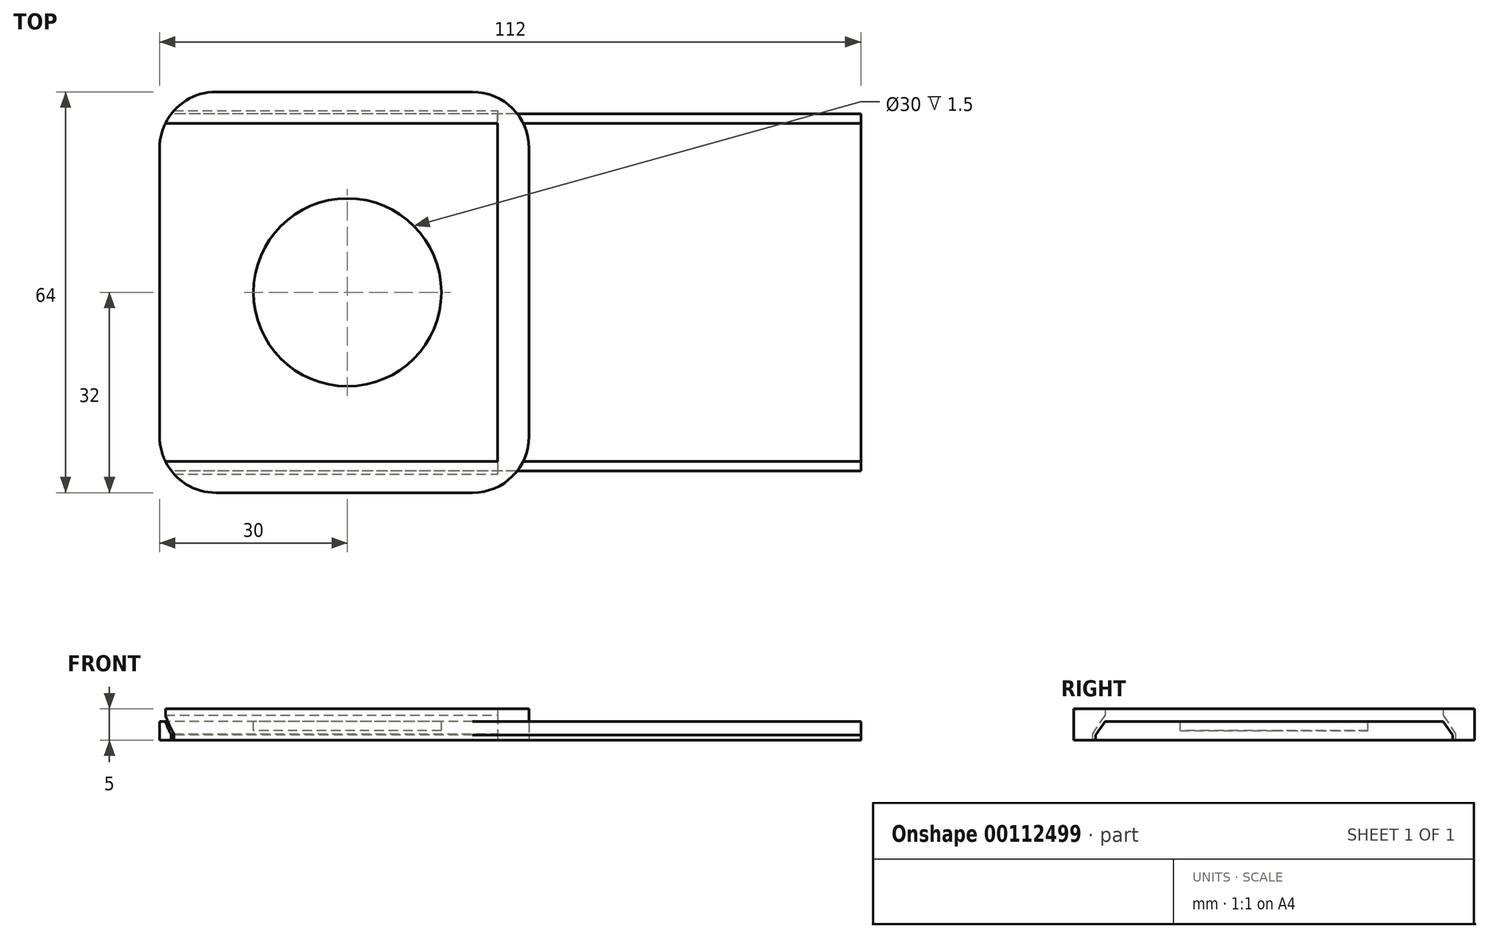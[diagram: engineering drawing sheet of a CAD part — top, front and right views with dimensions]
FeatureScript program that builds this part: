
annotation { "Feature Type Name" : "Feature", "Feature Type Description" : "" }
export const myFeature = defineFeature(function(context is Context, id is Id, definition is map)
    precondition{}
    {
        {
            var Q0;
            Q0=qCreatedBy(makeId("Top.planeOp"),FACE);
            var sketch = newSketch(context, id + "F0", { "sketchPlane" : qUnion([Q0])});
            skLineSegment(sketch, "E0.bottom", {"start": v(-59, 32) * mm, "end": v(59, 32) * mm});
            skLineSegment(sketch, "E0.top", {"start": v(-59, -32) * mm, "end": v(59, -32) * mm});
            skLineSegment(sketch, "E0.left", {"start": v(-59, 32) * mm, "end": v(-59, -32) * mm});
            skLineSegment(sketch, "E0.right", {"start": v(59, 32) * mm, "end": v(59, -32) * mm});
            skPoint(sketch, "E0.middle", {"position": v(0, 0) * mm});
            skSolve(sketch);
        }
        {
            var Q0;
            Q0=makeQuery(id+"F0.imprint","IMPRINT",FACE,{"disambiguationData":[TD([[makeQuery(id+"F0.imprint","IMPRINT",EDGE,{"derivedFrom":sQuery(id+"F0.wireOp",EDGE,"E0.bottom")}),-1.0]])]});
            extrude(context, id + "F1", {"entities" : qUnion([Q0]), "depth" : 82 * mm});
        }
        {
            var Q0;
            Q0=makeQuery(id+"F1.opExtrude","SWEPT_EDGE",EDGE,{"disambiguationData":[OSD([sQuery(id+"F0.wireOp",EDGE,"E0.top"),sQuery(id+"F0.wireOp",EDGE,"E0.left")])]});
            var Q1;
            Q1=makeQuery(id+"F1.opExtrude","SWEPT_EDGE",EDGE,{"disambiguationData":[OSD([sQuery(id+"F0.wireOp",EDGE,"E0.top"),sQuery(id+"F0.wireOp",EDGE,"E0.right")])]});
            var Q2;
            Q2=makeQuery(id+"F1.opExtrude","SWEPT_EDGE",EDGE,{"disambiguationData":[OSD([sQuery(id+"F0.wireOp",EDGE,"E0.bottom"),sQuery(id+"F0.wireOp",EDGE,"E0.right")])]});
            var Q3;
            Q3=makeQuery(id+"F1.opExtrude","SWEPT_EDGE",EDGE,{"disambiguationData":[OSD([sQuery(id+"F0.wireOp",EDGE,"E0.bottom"),sQuery(id+"F0.wireOp",EDGE,"E0.left")])]});
            fillet(context, id + "F2", {"entities" : qUnion([Q0, Q1, Q2, Q3]), "radius" : 9 * mm, "tangentPropagation" : true, "allowEdgeOverflow" : false});
        }
        {
            var Q0;
            Q0=makeQuery(id+"F1.opExtrude","CAP_FACE",FACE,{"disambiguationData":[OSD([sQuery(id+"F0.wireOp",EDGE,"E0.bottom"),sQuery(id+"F0.wireOp",EDGE,"E0.top"),sQuery(id+"F0.wireOp",EDGE,"E0.left"),sQuery(id+"F0.wireOp",EDGE,"E0.right")])],"isStart":false});
            shell(context, id + "F3", {"entities" : qUnion([Q0]), "thickness" : 5 * mm});
        }
        {
            var Q0;
            Q0=qCreatedBy(makeId("Right.planeOp"),FACE);
            var sketch = newSketch(context, id + "F4", { "sketchPlane" : qUnion([Q0])});
            skLineSegment(sketch, "E1", {"start": v(27, 82) * mm, "end": v(-27, 82) * mm});
            skLineSegment(sketch, "E2", {"start": v(29, 77) * mm, "end": v(-29, 77) * mm});
            skLineSegment(sketch, "E3", {"start": v(0, 77) * mm, "end": v(0, 82) * mm, "construction": true});
            skLineSegment(sketch, "E4", {"start": v(27, 82) * mm, "end": v(27, 81) * mm});
            skLineSegment(sketch, "E5", {"start": v(27, 81) * mm, "end": v(29, 78) * mm});
            skLineSegment(sketch, "E6", {"start": v(29, 78) * mm, "end": v(29, 77) * mm});
            skLineSegment(sketch, "E7", {"start": v(-27, 82) * mm, "end": v(-27, 81) * mm});
            skLineSegment(sketch, "E8", {"start": v(-27, 81) * mm, "end": v(-29, 78) * mm});
            skLineSegment(sketch, "E9", {"start": v(-29, 78) * mm, "end": v(-29, 77) * mm});
            skLineSegment(sketch, "E10", {"start": v(0, 77) * mm, "end": v(0, 0) * mm, "construction": true});
            skSolve(sketch);
        }
        {
            var Q0;
            Q0 = qSketchRegion(id + "F4", true);
            extrude(context, id + "F5", {"entities" : qUnion([Q0]), "operationType" : NewBodyOperationType.REMOVE, "oppositeDirection" : true, "depth" : 59 * mm});
        }
        {
            var Q0;
            Q0 = qSketchRegion(id + "F4", true);
            extrude(context, id + "F6", {"entities" : qUnion([Q0]), "operationType" : NewBodyOperationType.REMOVE, "depth" : 54 * mm});
        }
        {
            var Q0;
            Q0=qCreatedBy(makeId("Right.planeOp"),FACE);
            var sketch = newSketch(context, id + "F7", { "sketchPlane" : qUnion([Q0])});
            skLineSegment(sketch, "E11", {"start": v(28.5, 77) * mm, "end": v(-28.5, 77) * mm});
            skLineSegment(sketch, "E12", {"start": v(-28.5, 77) * mm, "end": v(-28.5, 77.8) * mm});
            skLineSegment(sketch, "E13", {"start": v(-28.5, 77.8) * mm, "end": v(-27, 80) * mm});
            skLineSegment(sketch, "E14", {"start": v(-27, 80) * mm, "end": v(27, 80) * mm});
            skLineSegment(sketch, "E15", {"start": v(27, 80) * mm, "end": v(28.5, 77.8) * mm});
            skLineSegment(sketch, "E16", {"start": v(28.5, 77.8) * mm, "end": v(28.5, 77) * mm});
            skLineSegment(sketch, "E17", {"start": v(0, 80) * mm, "end": v(0, 77) * mm, "construction": true});
            skLineSegment(sketch, "E18", {"start": v(0, 77) * mm, "end": v(0, 0) * mm, "construction": true});
            skSolve(sketch);
        }
        {
            var Q0;
            Q0 = qSketchRegion(id + "F7", true);
            extrude(context, id + "F8", {"entities" : qUnion([Q0]), "depth" : 112 * mm});
        }
        {
            var Q0;
            Q0=makeQuery(id+"F8.opExtrude","SWEPT_FACE",FACE,{"disambiguationData":[OSD([sQuery(id+"F7.wireOp",EDGE,"E11")])]});
            var sketch = newSketch(context, id + "F9", { "sketchPlane" : qUnion([Q0])});
            skLineSegment(sketch, "E19.bottom", {"start": v(9, 32) * mm, "end": v(118, 32) * mm});
            skLineSegment(sketch, "E19.top", {"start": v(9, -32) * mm, "end": v(118, -32) * mm});
            skLineSegment(sketch, "E19.left", {"start": v(0, 23) * mm, "end": v(0, -23) * mm});
            skLineSegment(sketch, "E19.right", {"start": v(118, 32) * mm, "end": v(118, -32) * mm});
            skPoint(sketch, "E19.middle", {"position": v(59, 0) * mm});
            skPoint(sketch, "E20.visualSharp", {"position": v(0, 32) * mm});
            skArc(sketch, "E20.filletArc", {"start": v(9, 32) * mm, "mid": v(2.64, 29.36) * mm, "end": v(0, 23) * mm});
            skPoint(sketch, "E21.visualSharp", {"position": v(0, -32) * mm});
            skArc(sketch, "E21.filletArc", {"start": v(0, -23) * mm, "mid": v(2.64, -29.36) * mm, "end": v(9, -32) * mm});
            skSolve(sketch);
        }
        {
            var Q0;
            Q0 = qSketchRegion(id + "F9", true);
            extrude(context, id + "F10", {"entities" : qUnion([Q0]), "operationType" : NewBodyOperationType.INTERSECT, "oppositeDirection" : true, "depth" : 25 * mm});
        }
        {
            var Q0;
            Q0=makeQuery(id+"F8.opExtrude","SWEPT_FACE",FACE,{"disambiguationData":[OSD([sQuery(id+"F7.wireOp",EDGE,"E14")])]});
            var sketch = newSketch(context, id + "F11", { "sketchPlane" : qUnion([Q0])});
            skCircle(sketch, "E22", {"center": v(30, 0) * mm, "radius": 15 * mm});
            skSolve(sketch);
        }
        {
            var Q0;
            Q0 = qSketchRegion(id + "F11", true);
            extrude(context, id + "F12", {"entities" : qUnion([Q0]), "operationType" : NewBodyOperationType.REMOVE, "oppositeDirection" : true, "depth" : 1.5 * mm});
        }
    });
